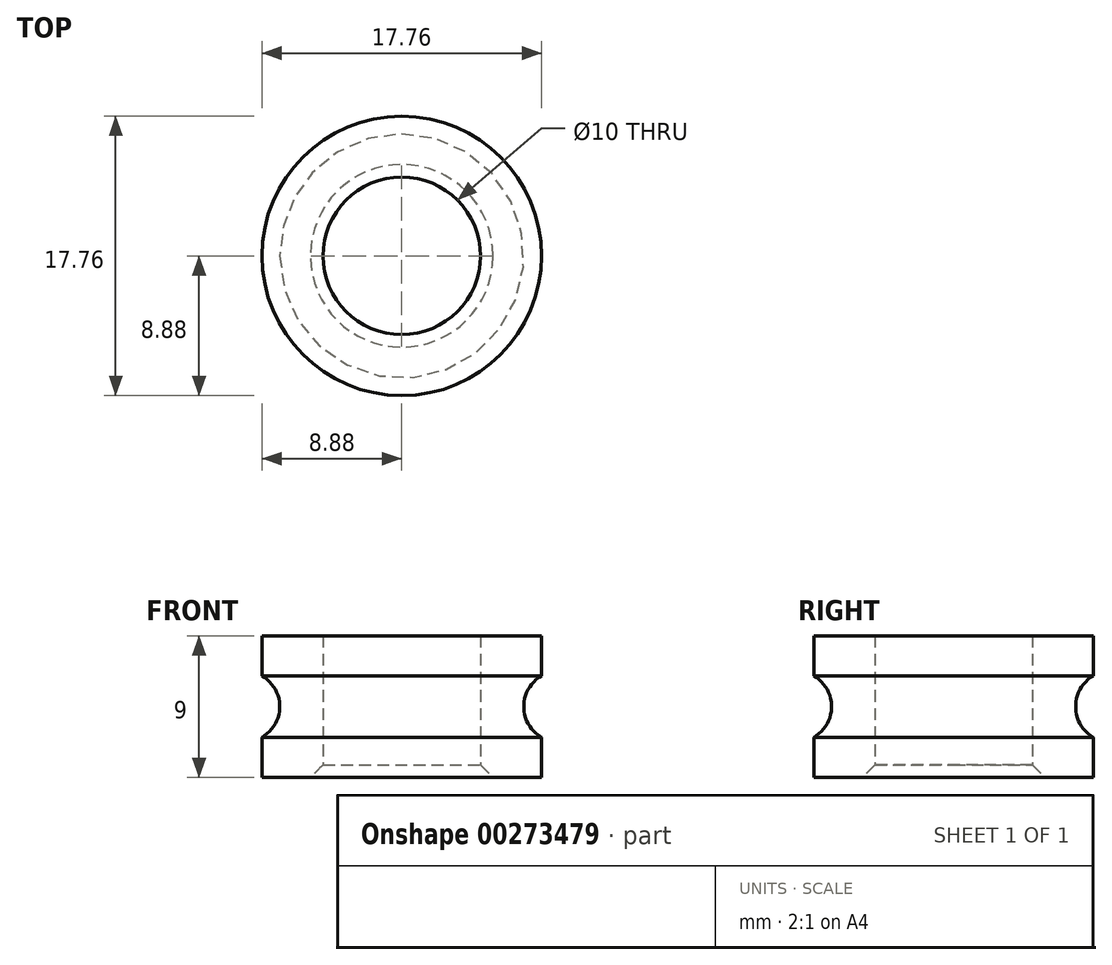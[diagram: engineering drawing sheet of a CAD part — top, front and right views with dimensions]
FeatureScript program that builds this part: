
annotation { "Feature Type Name" : "Feature", "Feature Type Description" : "" }
export const myFeature = defineFeature(function(context is Context, id is Id, definition is map)
    precondition{}
    {
        {
            var Q0;
            Q0=qCreatedBy(makeId("Front.planeOp"),FACE);
            var sketch = newSketch(context, id + "F0", { "sketchPlane" : qUnion([Q0])});
            skLineSegment(sketch, "E0", {"start": v(0, -65.9) * mm, "end": v(0, 112.28) * mm});
            skLineSegment(sketch, "E1", {"start": v(5, 0) * mm, "end": v(5, 9) * mm});
            skLineSegment(sketch, "E2", {"start": v(5, 0) * mm, "end": v(8.87, 0) * mm});
            skLineSegment(sketch, "E3", {"start": v(8.87, 0) * mm, "end": v(8.87, 2.55) * mm});
            skLineSegment(sketch, "E4", {"start": v(8.87, 9) * mm, "end": v(5, 9) * mm});
            skArc(sketch, "E5", {"start": v(8.87, 6.45) * mm, "mid": v(7.75, 4.5) * mm, "end": v(8.87, 2.55) * mm});
            skLineSegment(sketch, "E6.trimOffspring", {"start": v(8.87, 6.45) * mm, "end": v(8.87, 9) * mm});
            skPoint(sketch, "E7.start.orphan", {"position": v(5, 4.5) * mm});
            skSolve(sketch);
        }
        {
            var Q0;
            Q0=makeQuery(id+"F0.imprint","IMPRINT",FACE,{"disambiguationData":[TD([[makeQuery(id+"F0.imprint","IMPRINT",EDGE,{"derivedFrom":sQuery(id+"F0.wireOp",EDGE,"E1")}),-1.0]])]});
            var Q1;
            Q1=sQuery(id+"F0.wireOp",EDGE,"E0");
            revolve(context, id + "F1", {"entities" : qUnion([Q0]), "axis" : qUnion([Q1]), "revolveType" : RevolveType.FULL});
        }
        {
            var Q0;
            Q0=makeQuery(id+"F1.opRevolve","SWEPT_EDGE",EDGE,{"disambiguationData":[OSD([sQuery(id+"F0.wireOp",EDGE,"E1"),sQuery(id+"F0.wireOp",EDGE,"E2")])]});
            chamfer(context, id + "F2", {"entities" : qUnion([Q0]), "width" : .8 * mm, "tangentPropagation" : true});
        }
    });
